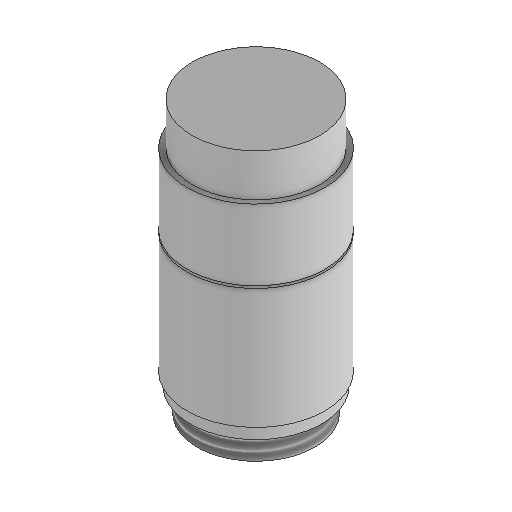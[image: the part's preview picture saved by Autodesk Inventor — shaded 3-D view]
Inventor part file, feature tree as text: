
AUTODESK INVENTOR PART (.ipt)
format: ipt  version: 2024.1 (Build 281209000, 209)  size: 139,264 bytes
history: native  units: mm
features: revolve x1, thread x1, sketch x1
ambient origin geometry x8: Origin, YZ Plane, XZ Plane, XY Plane, X Axis, Y Axis, Z Axis, Center Point
bodies: Volumenkörper1 (feature_tree)
feature tree (3):
  revolve  "Umdrehung1"
  thread  "Gewinde1"  [1 undecoded]
  sketch  "Skizze1"  dims[d1=9.0mm d2=90.0deg d3=1.1mm d4=270.0deg d5=0.5mm d6=1.0mm d7=15.0mm d8=360.0deg d9=13.95mm d10=2.7mm d11=5.0mm d12=0.0mm d13=12.5mm d14=5.0mm]
note: 1 required parameter value undecoded (feature->parameter linkage not recoverable at this tier; creation-order binding heuristic only, values carry confidence <= 0.55)
